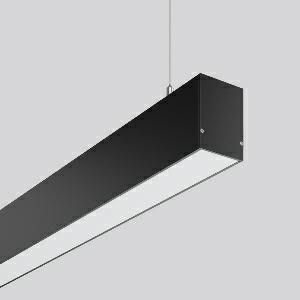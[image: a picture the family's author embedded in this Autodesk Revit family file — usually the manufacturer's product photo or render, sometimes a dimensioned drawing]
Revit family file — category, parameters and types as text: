
# Revit family: less_is_more_50_312311_003_1_99da
name_source: partatom
category: Lighting Fixtures
units: mm (PartAtom-declared; Revit-internal decimal feet)

## family parameters
Cut with Voids When Loaded = No
Host = Face
Light Source = No
Part Type = Normal
Room Calculation Point = No
Round Connector Dimension = Use Diameter
Shared = No

## types (1)
- LESS IS MORE 50 (1 x LED Modul 840, 2400 lm, 4000)
    Apparent Load = 22 VA
    CIE Flux Codes = 48 79 95 100 100
    Color Rendering = 80
    Color Temperature = 4000
    Default Elevation = 1800 mm
    Description = Series: LESS IS MORE 50
Linear pendant luminaire for aesthetically sophisticated lighting. Housing: extruded aluminium profile, powder-coated. End cap aluminium powder-coated. Canopy made of aluminium, powder-coated. Diffuser made of non-yellowing plastic (PMMA), opal. Direct light emission. Suitable for pendant. 2-point steel cable suspension freely positionable and infinitely height-adjustable. Special lengths available on request. LED unit with integrated converter interchangeable and removable. Suitable for through-wiring. With sensors or as a safety luminaire on request. 
Colour: deep black, matt (RAL 9005)
Length: 847 mm
Width: 57 mm
Height: 75 mm
Suspension length: 2000 mm
Lamp: LED
Socket: without socket
Colour temperature: 4000K
Colour rendering index (CRI): 80
System power: 22 W
Rated luminous flux: 2400 lm
Luminous efficiency: 109 lm/W
Control gear: Regulated power supply
Protection class: I
Type of protection: IP 20
    Height = 75 mm
    Lamp = 1 x LED Modul 840
    Lamp Light Flux = 2400 lm
    Lamp count = 1
    Length = 847 mm
    Lifetime = 50000 h
    Luminous efficacy = 109 lm/W
    Manufacturer = RZB
    ModVariant = No
    Model = 312311.003.1
    Mounting Place = Ceiling
    Mounting Type = Pendant
    Number of Poles = 1
    OnlyDefault = Yes
    Power Factor = 1
    Product Name = LESS IS MORE 50
    Product group = Pendant LED linear luminaires
    ProductGroupID = 907
    Protection Class = Protection class I
    Protection Degree = IP 20
    RLX_Detail_Level = 1
    RLX_Emergency_Light_Flux = 0 lm
    RLX_Emergency_Type = 0
    RLX_Emergency_Type_DB = No
    RlxData = <blob elided: 28881 chars, md5=571e739d>
    Socket = socket
    Standby Power = 0 W
    System Light Flux = 2400 lm
    System Power = 22 W
    Type Comments = Product without accessories
    Type Image = 312318.003.jpg
    URL = http://relux.com
    VarID = ---
    Voltage = 230 V
    Voltage Range = 220-240 V
    Weight = 0.00 kg
    Width = 57 mm

## geometry (parser evidence)
native form markers: Blend x4, Sweep x10
no freeform markers — native parametric forms only
